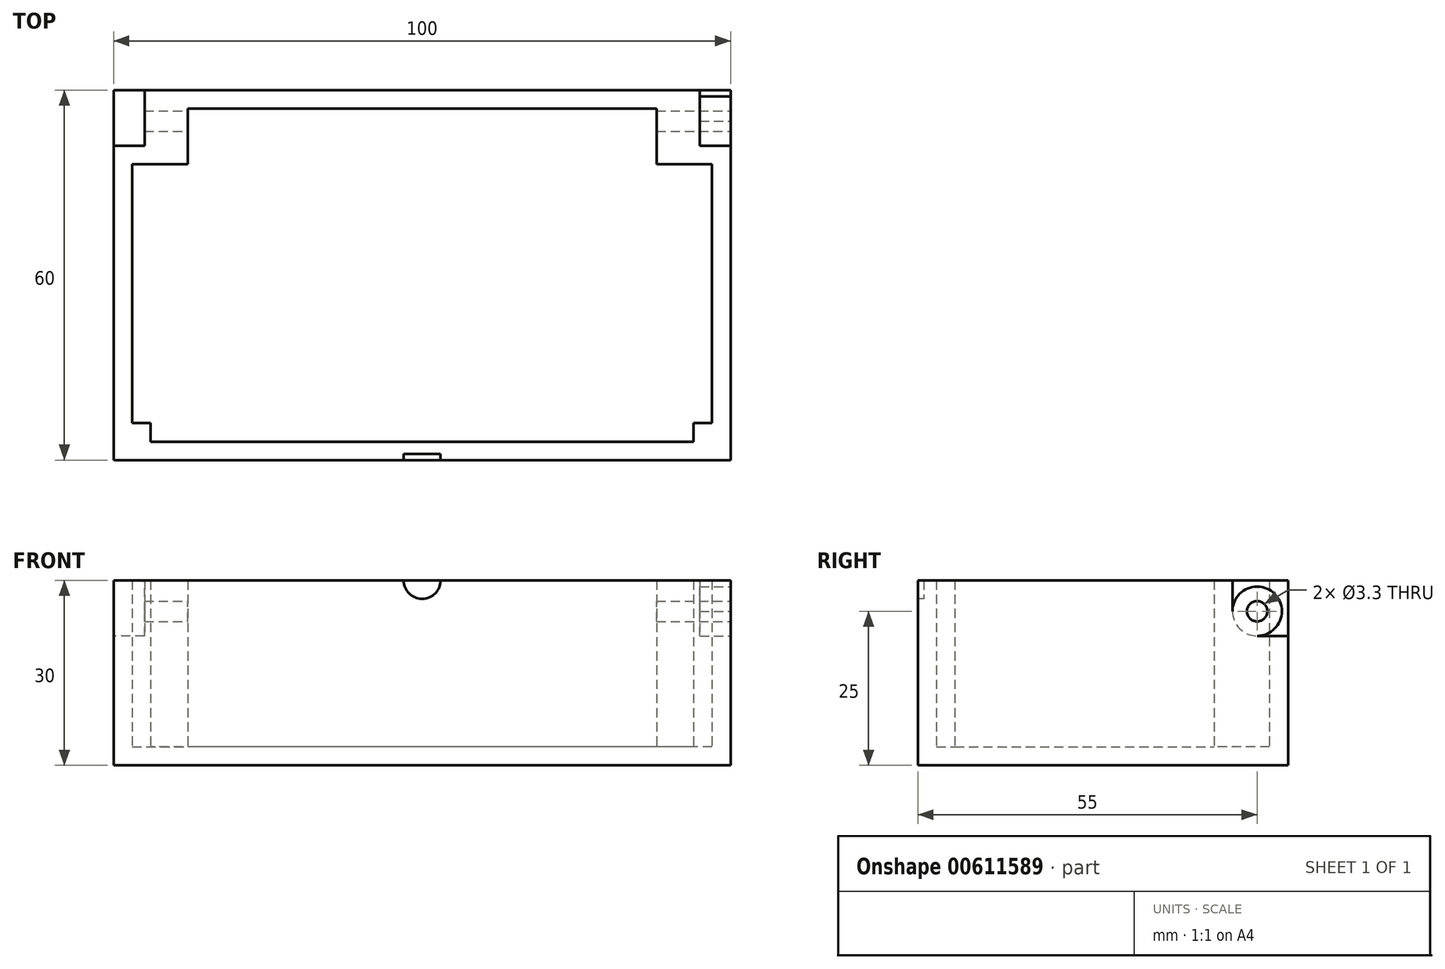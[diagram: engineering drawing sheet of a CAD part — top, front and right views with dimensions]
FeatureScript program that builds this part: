
annotation { "Feature Type Name" : "Feature", "Feature Type Description" : "" }
export const myFeature = defineFeature(function(context is Context, id is Id, definition is map)
    precondition{}
    {
        {
            var Q0;
            Q0=qCreatedBy(makeId("Top.planeOp"),FACE);
            var sketch = newSketch(context, id + "F0", { "sketchPlane" : qUnion([Q0])});
            skLineSegment(sketch, "E0.bottom", {"start": v(50, -30) * mm, "end": v(-50, -30) * mm});
            skLineSegment(sketch, "E0.top", {"start": v(50, 30) * mm, "end": v(-50, 30) * mm});
            skLineSegment(sketch, "E0.left", {"start": v(50, -30) * mm, "end": v(50, 30) * mm});
            skLineSegment(sketch, "E0.right", {"start": v(-50, -30) * mm, "end": v(-50, 30) * mm});
            skPoint(sketch, "E0.middle", {"position": v(0, 0) * mm});
            skSolve(sketch);
        }
        {
            var Q0;
            Q0=makeQuery(id+"F0.imprint","IMPRINT",FACE,{"disambiguationData":[TD([[makeQuery(id+"F0.imprint","IMPRINT",EDGE,{"derivedFrom":sQuery(id+"F0.wireOp",EDGE,"E0.bottom")}),-1.0]])]});
            extrude(context, id + "F1", {"entities" : qUnion([Q0]), "depth" : 30 * mm, "offsetDistance" : 25 * mm});
        }
        {
            var Q0;
            Q0=makeQuery(id+"F1.opExtrude","CAP_FACE",FACE,{"disambiguationData":[OSD([sQuery(id+"F0.wireOp",EDGE,"E0.bottom"),sQuery(id+"F0.wireOp",EDGE,"E0.top"),sQuery(id+"F0.wireOp",EDGE,"E0.left"),sQuery(id+"F0.wireOp",EDGE,"E0.right")])],"isStart":false});
            shell(context, id + "F2", {"entities" : qUnion([Q0]), "thickness" : 3 * mm});
        }
        {
            var Q0;
            Q0=makeQuery(id+"F2.opShell","OFFSET_FACE",FACE,{"disambiguationData":[OSD([sQuery(id+"F0.wireOp",EDGE,"E0.bottom"),sQuery(id+"F0.wireOp",EDGE,"E0.top"),sQuery(id+"F0.wireOp",EDGE,"E0.left"),sQuery(id+"F0.wireOp",EDGE,"E0.right")])]});
            var sketch = newSketch(context, id + "F3", { "sketchPlane" : qUnion([Q0])});
            skLineSegment(sketch, "E1.bottom", {"start": v(-47, 27) * mm, "end": v(-38, 27) * mm});
            skLineSegment(sketch, "E1.top", {"start": v(-47, 18) * mm, "end": v(-38, 18) * mm});
            skLineSegment(sketch, "E1.left", {"start": v(-47, 27) * mm, "end": v(-47, 18) * mm});
            skLineSegment(sketch, "E1.right", {"start": v(-38, 27) * mm, "end": v(-38, 18) * mm});
            skLineSegment(sketch, "E2.bottom", {"start": v(47, 27) * mm, "end": v(38, 27) * mm});
            skLineSegment(sketch, "E2.top", {"start": v(47, 18) * mm, "end": v(38, 18) * mm});
            skLineSegment(sketch, "E2.left", {"start": v(47, 27) * mm, "end": v(47, 18) * mm});
            skLineSegment(sketch, "E2.right", {"start": v(38, 27) * mm, "end": v(38, 18) * mm});
            skLineSegment(sketch, "E3.bottom", {"start": v(-47, -27) * mm, "end": v(-44, -27) * mm});
            skLineSegment(sketch, "E3.top", {"start": v(-47, -24) * mm, "end": v(-44, -24) * mm});
            skLineSegment(sketch, "E3.left", {"start": v(-47, -27) * mm, "end": v(-47, -24) * mm});
            skLineSegment(sketch, "E3.right", {"start": v(-44, -27) * mm, "end": v(-44, -24) * mm});
            skLineSegment(sketch, "E4.bottom", {"start": v(47, -27) * mm, "end": v(44, -27) * mm});
            skLineSegment(sketch, "E4.top", {"start": v(47, -24) * mm, "end": v(44, -24) * mm});
            skLineSegment(sketch, "E4.left", {"start": v(47, -27) * mm, "end": v(47, -24) * mm});
            skLineSegment(sketch, "E4.right", {"start": v(44, -27) * mm, "end": v(44, -24) * mm});
            skSolve(sketch);
        }
        {
            var Q0;
            Q0=makeQuery(id+"F3.imprint","IMPRINT",FACE,{"disambiguationData":[TD([[makeQuery(id+"F3.imprint","IMPRINT",EDGE,{"derivedFrom":sQuery(id+"F3.wireOp",EDGE,"E1.bottom")}),1.0]])]});
            var Q1;
            Q1=makeQuery(id+"F3.imprint","IMPRINT",FACE,{"disambiguationData":[TD([[makeQuery(id+"F3.imprint","IMPRINT",EDGE,{"derivedFrom":sQuery(id+"F3.wireOp",EDGE,"E2.bottom")}),1.0]])]});
            var Q2;
            Q2=makeQuery(id+"F3.imprint","IMPRINT",FACE,{"disambiguationData":[TD([[makeQuery(id+"F3.imprint","IMPRINT",EDGE,{"derivedFrom":sQuery(id+"F3.wireOp",EDGE,"E4.bottom")}),-1.0]])]});
            var Q3;
            Q3=makeQuery(id+"F3.imprint","IMPRINT",FACE,{"disambiguationData":[TD([[makeQuery(id+"F3.imprint","IMPRINT",EDGE,{"derivedFrom":sQuery(id+"F3.wireOp",EDGE,"E3.bottom")}),-1.0]])]});
            extrude(context, id + "F4", {"entities" : qUnion([Q0, Q1, Q2, Q3]), "operationType" : NewBodyOperationType.ADD, "depth" : 27 * mm, "offsetDistance" : 25 * mm});
        }
        {
            var Q0;
            Q0=makeQuery(id+"F1.opExtrude","SWEPT_FACE",FACE,{"disambiguationData":[OSD([sQuery(id+"F0.wireOp",EDGE,"E0.left")])]});
            var sketch = newSketch(context, id + "F5", { "sketchPlane" : qUnion([Q0])});
            skPoint(sketch, "E5", {"position": v(25, 25) * mm});
            skCircle(sketch, "E6", {"center": v(25, 25) * mm, "radius": 4 * mm});
            skLineSegment(sketch, "E7", {"start": v(21, 25) * mm, "end": v(21, 30) * mm});
            skLineSegment(sketch, "E8", {"start": v(25, 21) * mm, "end": v(30, 21) * mm});
            skCircle(sketch, "E9", {"center": v(25, 25) * mm, "radius": 1.65 * mm});
            skSolve(sketch);
        }
        {
            var Q0;
            Q0=makeQuery(id+"F5.imprint","IMPRINT",FACE,{"disambiguationData":[TD([[makeQuery(id+"F5.imprint","IMPRINT",EDGE,{"derivedFrom":sQuery(id+"F5.wireOp",EDGE,"E9")}),1.0]])]});
            extrude(context, id + "F6", {"entities" : qUnion([Q0]), "operationType" : NewBodyOperationType.REMOVE, "endBound" : BoundingType.THROUGH_ALL, "oppositeDirection" : true, "depth" : 25 * mm, "offsetDistance" : 25 * mm});
        }
        {
            var Q0;
            Q0=makeQuery(id+"F1.opExtrude","SWEPT_FACE",FACE,{"disambiguationData":[OSD([sQuery(id+"F0.wireOp",EDGE,"E0.left")])]});
            var sketch = newSketch(context, id + "F7", { "sketchPlane" : qUnion([Q0])});
            skPoint(sketch, "E10", {"position": v(25, 25) * mm});
            skCircle(sketch, "E11", {"center": v(25, 25) * mm, "radius": 4 * mm});
            skLineSegment(sketch, "E12", {"start": v(21, 25) * mm, "end": v(21, 30) * mm});
            skLineSegment(sketch, "E13", {"start": v(25, 21) * mm, "end": v(30, 21) * mm});
            skSolve(sketch);
        }
        {
            var Q0;
            Q0=makeQuery(id+"F7.imprint","IMPRINT",FACE,{"disambiguationData":[TD([[makeQuery(id+"F7.imprint","IMPRINT",EDGE,{"derivedFrom":makeQuery(id+"F6.boolean.opBoolean","COPY",EDGE,{"derivedFrom":makeQuery(id+"F6.opExtrude","CAP_EDGE",EDGE,{"disambiguationData":[OSD([sQuery(id+"F5.wireOp",EDGE,"E9")])],"isStart":true})})}),-1.0]])]});
            var Q1;
            {var subQ5=sQuery(id+"F7.wireOp",EDGE,"E12");Q1=makeQuery(id+"F7.imprint","IMPRINT",FACE,{"disambiguationData":[TD([[makeQuery(id+"F7.imprint","IMPRINT",EDGE,{"derivedFrom":subQ5}),-1.0]])]});}
            extrude(context, id + "F8", {"entities" : qUnion([Q0, Q1]), "operationType" : NewBodyOperationType.REMOVE, "oppositeDirection" : true, "depth" : 5 * mm, "offsetDistance" : 25 * mm});
        }
        {
            var Q0;
            Q0=makeQuery(id+"F1.opExtrude","SWEPT_FACE",FACE,{"disambiguationData":[OSD([sQuery(id+"F0.wireOp",EDGE,"E0.right")])]});
            var sketch = newSketch(context, id + "F9", { "sketchPlane" : qUnion([Q0])});
            skPoint(sketch, "E14", {"position": v(-25, 25) * mm});
            skCircle(sketch, "E15", {"center": v(-25, 25) * mm, "radius": 4 * mm});
            skLineSegment(sketch, "E16", {"start": v(-21, 25) * mm, "end": v(-21, 30) * mm});
            skLineSegment(sketch, "E17", {"start": v(-25, 21) * mm, "end": v(-30, 21) * mm});
            skSolve(sketch);
        }
        {
            var Q0;
            Q0=makeQuery(id+"F9.imprint","IMPRINT",FACE,{"disambiguationData":[TD([[makeQuery(id+"F9.imprint","IMPRINT",EDGE,{"derivedFrom":makeQuery(id+"F6.boolean.opBoolean","INTERSECT",EDGE,{"derivedFrom":[makeQuery(id+"F1.opExtrude","SWEPT_FACE",FACE,{"disambiguationData":[OSD([sQuery(id+"F0.wireOp",EDGE,"E0.right")])]}),makeQuery(id+"F6.opExtrude","SWEPT_FACE",FACE,{"disambiguationData":[OSD([sQuery(id+"F5.wireOp",EDGE,"E9")])]})]})}),-1.0]])]});
            var Q1;
            {var subQ5=sQuery(id+"F9.wireOp",EDGE,"E16");Q1=makeQuery(id+"F9.imprint","IMPRINT",FACE,{"disambiguationData":[TD([[makeQuery(id+"F9.imprint","IMPRINT",EDGE,{"derivedFrom":subQ5}),1.0]])]});}
            extrude(context, id + "F10", {"entities" : qUnion([Q0, Q1]), "operationType" : NewBodyOperationType.REMOVE, "oppositeDirection" : true, "depth" : 5 * mm, "offsetDistance" : 25 * mm});
        }
        {
            var Q0;
            Q0=makeQuery(id+"F1.opExtrude","SWEPT_FACE",FACE,{"disambiguationData":[OSD([sQuery(id+"F0.wireOp",EDGE,"E0.bottom")])]});
            var sketch = newSketch(context, id + "F11", { "sketchPlane" : qUnion([Q0])});
            skPoint(sketch, "E18", {"position": v(0, 30) * mm});
            skCircle(sketch, "E19", {"center": v(0, 30) * mm, "radius": 3 * mm});
            skSolve(sketch);
        }
        {
            var Q0;
            {var subQ0=sQuery(id+"F11.wireOp",EDGE,"E19");var subQ1=makeQuery(id+"F1.opExtrude","CAP_EDGE",EDGE,{"disambiguationData":[OSD([sQuery(id+"F0.wireOp",EDGE,"E0.bottom")])],"isStart":false});var subQ2=makeQuery(id+"F11.imprint","INTERSECT",VERTEX,{"disambiguationData":[OD(0.0)],"derivedFrom":[subQ1,subQ0]});Q0=makeQuery(id+"F11.imprint","IMPRINT",FACE,{"disambiguationData":[TD([[makeQuery(id+"F11.imprint","IMPRINT",EDGE,{"disambiguationData":[TD([[subQ2,1.0]])],"derivedFrom":subQ0}),1.0]])]});}
            extrude(context, id + "F12", {"entities" : qUnion([Q0]), "operationType" : NewBodyOperationType.REMOVE, "oppositeDirection" : true, "depth" : 1 * mm, "offsetDistance" : 25 * mm});
        }
    });
